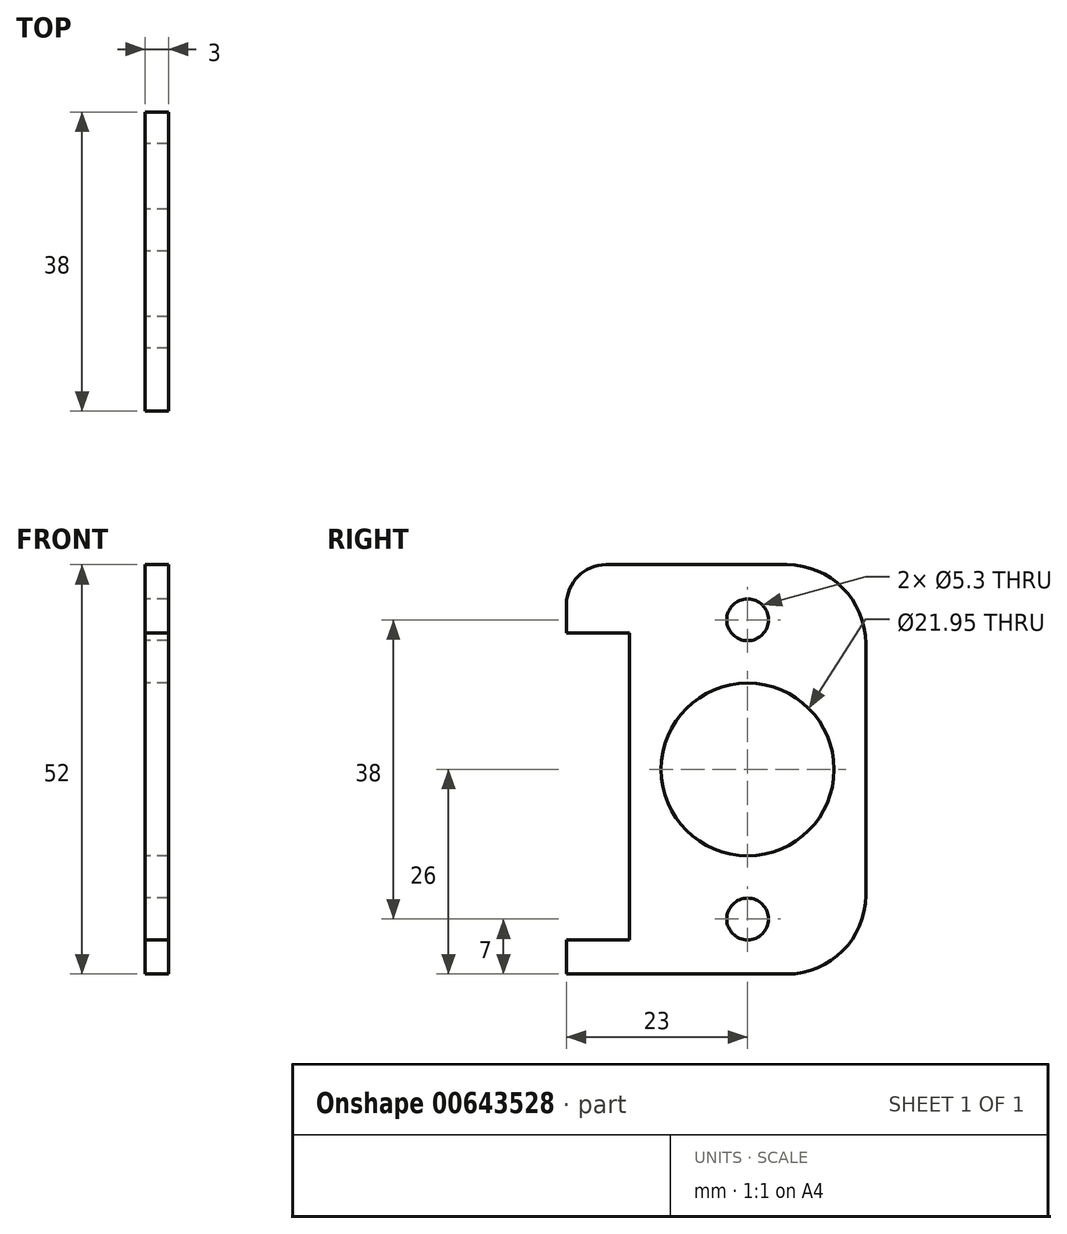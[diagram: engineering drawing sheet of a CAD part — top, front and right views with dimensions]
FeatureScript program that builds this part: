
annotation { "Feature Type Name" : "Feature", "Feature Type Description" : "" }
export const myFeature = defineFeature(function(context is Context, id is Id, definition is map)
    precondition{}
    {
        {
            var Q0;
            Q0=qCreatedBy(makeId("Right.planeOp"),FACE);
            var sketch = newSketch(context, id + "F0", { "sketchPlane" : qUnion([Q0])});
            skLineSegment(sketch, "E0.bottom", {"start": v(19, 26) * mm, "end": v(-19, 26) * mm, "construction": true});
            skLineSegment(sketch, "E0.top", {"start": v(19, -26) * mm, "end": v(-19, -26) * mm, "construction": true});
            skLineSegment(sketch, "E0.left", {"start": v(19, 26) * mm, "end": v(19, -26) * mm, "construction": true});
            skLineSegment(sketch, "E0.right", {"start": v(-19, 26) * mm, "end": v(-19, -26) * mm, "construction": true});
            skPoint(sketch, "E0.middle", {"position": v(0, 0) * mm});
            skLineSegment(sketch, "E1", {"start": v(-19, 21) * mm, "end": v(-19, 17.3) * mm});
            skLineSegment(sketch, "E2", {"start": v(-19, 17.3) * mm, "end": v(-11, 17.3) * mm});
            skLineSegment(sketch, "E3", {"start": v(-11, 17.3) * mm, "end": v(-11, -21.65) * mm});
            skLineSegment(sketch, "E4", {"start": v(-11, -21.65) * mm, "end": v(-19, -21.65) * mm});
            skLineSegment(sketch, "E5", {"start": v(-19, -21.65) * mm, "end": v(-19, -26) * mm});
            skLineSegment(sketch, "E6", {"start": v(19, -16) * mm, "end": v(19, 16) * mm});
            skLineSegment(sketch, "E7", {"start": v(9, 26) * mm, "end": v(-14, 26) * mm});
            skLineSegment(sketch, "E8", {"start": v(-19, -26) * mm, "end": v(9, -26) * mm});
            skPoint(sketch, "E9.visualSharp", {"position": v(19, 26) * mm});
            skArc(sketch, "E9.filletArc", {"start": v(19, 16) * mm, "mid": v(16.07, 23.07) * mm, "end": v(9, 26) * mm});
            skPoint(sketch, "E10.visualSharp", {"position": v(19, -26) * mm});
            skArc(sketch, "E10.filletArc", {"start": v(9, -26) * mm, "mid": v(16.07, -23.07) * mm, "end": v(19, -16) * mm});
            skCircle(sketch, "E11", {"center": v(4, 19) * mm, "radius": 2.65 * mm});
            skCircle(sketch, "E12", {"center": v(4, -19) * mm, "radius": 2.65 * mm});
            skLineSegment(sketch, "E13", {"start": v(4, -19) * mm, "end": v(4, 19) * mm, "construction": true});
            skCircle(sketch, "E14", {"center": v(4, 0) * mm, "radius": 4.25 * mm, "construction": true});
            skCircle(sketch, "E15", {"center": v(4, 19) * mm, "radius": 4.97 * mm, "construction": true});
            skCircle(sketch, "E16", {"center": v(4, -19) * mm, "radius": 4.97 * mm, "construction": true});
            skCircle(sketch, "E17", {"center": v(4, 0) * mm, "radius": 4.97 * mm, "construction": true});
            skCircle(sketch, "E18", {"center": v(4, 0) * mm, "radius": 10.97 * mm});
            skPoint(sketch, "E19.visualSharp", {"position": v(-19, 26) * mm});
            skArc(sketch, "E19.filletArc", {"start": v(-14, 26) * mm, "mid": v(-17.54, 24.54) * mm, "end": v(-19, 21) * mm});
            skSolve(sketch);
        }
        {
            var Q0;
            Q0=qSketchRegion(id+"F0",true);
            extrude(context, id + "F1", {"entities" : qUnion([Q0]), "depth" : 3 * mm, "offsetDistance" : 25 * mm});
        }
    });
